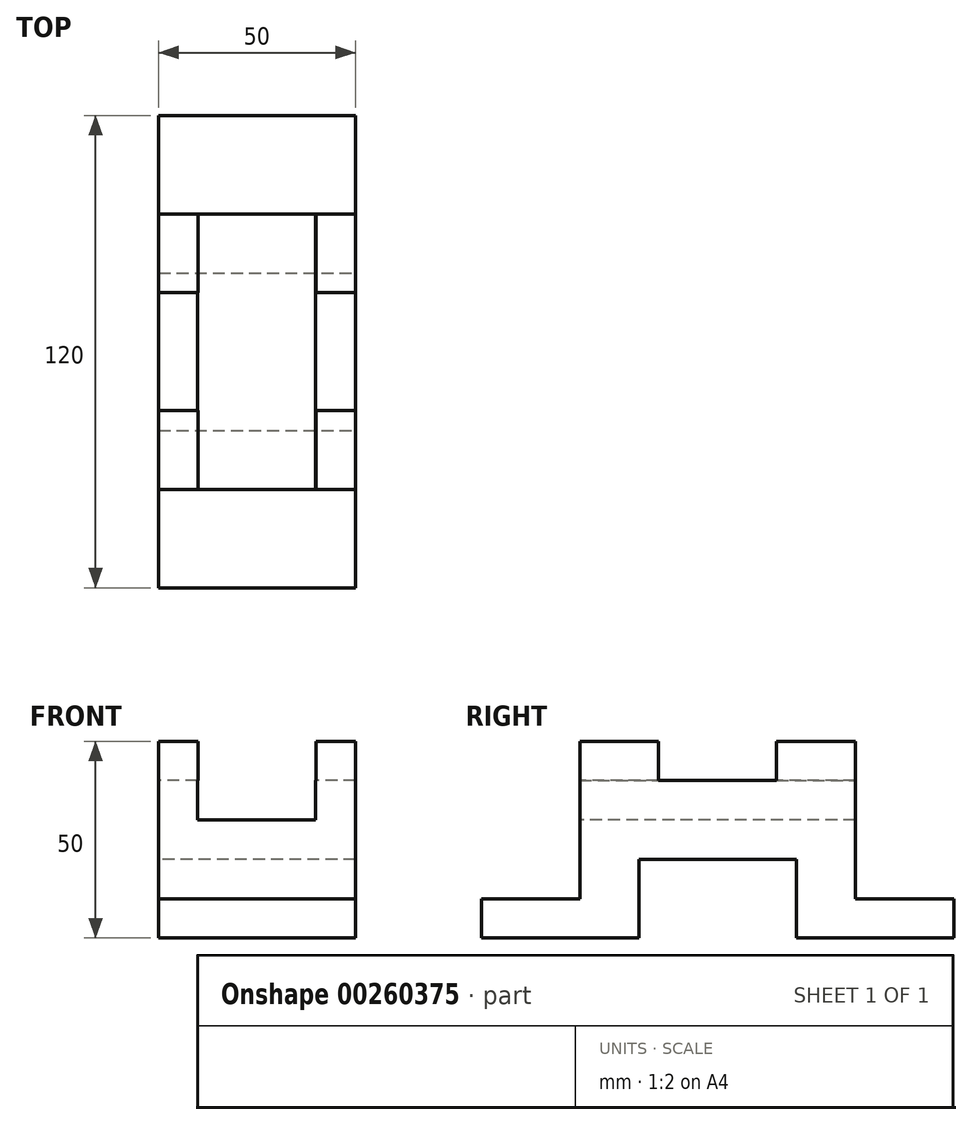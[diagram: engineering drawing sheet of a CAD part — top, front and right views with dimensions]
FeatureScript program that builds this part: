
annotation { "Feature Type Name" : "Feature", "Feature Type Description" : "" }
export const myFeature = defineFeature(function(context is Context, id is Id, definition is map)
    precondition{}
    {
        {
            assignVariable(context, id + "F0", {"name" : "B", "anyValue" : 50 * mm});
        }
        {
            var Q0;
            Q0=qCreatedBy(makeId("Top.planeOp"),FACE);
            var sketch = newSketch(context, id + "F1", { "sketchPlane" : qUnion([Q0])});
            skLineSegment(sketch, "E0.bottom", {"start": v(25, -60) * mm, "end": v(-25, -60) * mm});
            skLineSegment(sketch, "E0.top", {"start": v(25, 60) * mm, "end": v(-25, 60) * mm});
            skLineSegment(sketch, "E0.left", {"start": v(25, -60) * mm, "end": v(25, 60) * mm});
            skLineSegment(sketch, "E0.right", {"start": v(-25, -60) * mm, "end": v(-25, 60) * mm});
            skPoint(sketch, "E0.middle", {"position": v(0, 0) * mm});
            skSolve(sketch);
        }
        {
            var Q0;
            Q0=makeQuery(id+"F1.imprint","IMPRINT",FACE,{"disambiguationData":[TD([[makeQuery(id+"F1.imprint","IMPRINT",EDGE,{"derivedFrom":sQuery(id+"F1.wireOp",EDGE,"E0.bottom")}),-1.0]])]});
            extrude(context, id + "F2", {"entities" : qUnion([Q0]), "depth" : getVariable(context, 'B'), "symmetric" : true});
        }
        {
            var Q0;
            Q0=makeQuery(id+"F2.opExtrude","SWEPT_FACE",FACE,{"disambiguationData":[OSD([sQuery(id+"F1.wireOp",EDGE,"E0.right")])]});
            var sketch = newSketch(context, id + "F3", { "sketchPlane" : qUnion([Q0])});
            skLineSegment(sketch, "E1.bottom", {"start": v(20, -45) * mm, "end": v(-20, -45) * mm});
            skLineSegment(sketch, "E1.top", {"start": v(20, -5) * mm, "end": v(-20, -5) * mm});
            skLineSegment(sketch, "E1.left", {"start": v(20, -45) * mm, "end": v(20, -5) * mm});
            skLineSegment(sketch, "E1.right", {"start": v(-20, -45) * mm, "end": v(-20, -5) * mm});
            skPoint(sketch, "E1.middle", {"position": v(0, -25) * mm});
            skSolve(sketch);
        }
        {
            var Q0;
            Q0 = qSketchRegion(id + "F3", true);
            extrude(context, id + "F4", {"entities" : qUnion([Q0]), "operationType" : NewBodyOperationType.REMOVE, "oppositeDirection" : true, "depth" : 50 * mm});
        }
        {
            var Q0;
            Q0=makeQuery(id+"F2.opExtrude","SWEPT_FACE",FACE,{"disambiguationData":[OSD([sQuery(id+"F1.wireOp",EDGE,"E0.right")])]});
            var sketch = newSketch(context, id + "F5", { "sketchPlane" : qUnion([Q0])});
            skLineSegment(sketch, "E2.bottom", {"start": v(-60, 25) * mm, "end": v(-35, 25) * mm});
            skLineSegment(sketch, "E2.top", {"start": v(-60, -15) * mm, "end": v(-35, -15) * mm});
            skLineSegment(sketch, "E2.left", {"start": v(-60, 25) * mm, "end": v(-60, -15) * mm});
            skLineSegment(sketch, "E2.right", {"start": v(-35, 25) * mm, "end": v(-35, -15) * mm});
            skSolve(sketch);
        }
        {
            var Q0;
            Q0=makeQuery(id+"F5.imprint","IMPRINT",FACE,{"disambiguationData":[TD([[makeQuery(id+"F5.imprint","IMPRINT",EDGE,{"derivedFrom":sQuery(id+"F5.wireOp",EDGE,"E2.bottom")}),1.0]])]});
            extrude(context, id + "F6", {"entities" : qUnion([Q0]), "operationType" : NewBodyOperationType.REMOVE, "oppositeDirection" : true, "depth" : 50 * mm});
        }
        {
            var Q0;
            Q0=makeQuery(id+"F2.opExtrude","SWEPT_FACE",FACE,{"disambiguationData":[OSD([sQuery(id+"F1.wireOp",EDGE,"E0.right")])]});
            var sketch = newSketch(context, id + "F7", { "sketchPlane" : qUnion([Q0])});
            skLineSegment(sketch, "E3.bottom", {"start": v(60, 25) * mm, "end": v(35, 25) * mm});
            skLineSegment(sketch, "E3.top", {"start": v(60, -15) * mm, "end": v(35, -15) * mm});
            skLineSegment(sketch, "E3.left", {"start": v(60, 25) * mm, "end": v(60, -15) * mm});
            skLineSegment(sketch, "E3.right", {"start": v(35, 25) * mm, "end": v(35, -15) * mm});
            skSolve(sketch);
        }
        {
            var Q0;
            Q0=makeQuery(id+"F7.imprint","IMPRINT",FACE,{"disambiguationData":[TD([[makeQuery(id+"F7.imprint","IMPRINT",EDGE,{"derivedFrom":sQuery(id+"F7.wireOp",EDGE,"E3.bottom")}),1.0]])]});
            extrude(context, id + "F8", {"entities" : qUnion([Q0]), "operationType" : NewBodyOperationType.REMOVE, "oppositeDirection" : true, "depth" : 50 * mm});
        }
        {
            var Q0;
            Q0=makeQuery(id+"F2.opExtrude","SWEPT_FACE",FACE,{"disambiguationData":[OSD([sQuery(id+"F1.wireOp",EDGE,"E0.right")])]});
            var sketch = newSketch(context, id + "F9", { "sketchPlane" : qUnion([Q0])});
            skLineSegment(sketch, "E4.bottom", {"start": v(15, 15) * mm, "end": v(-15, 15) * mm});
            skLineSegment(sketch, "E4.top", {"start": v(15, 35) * mm, "end": v(-15, 35) * mm});
            skLineSegment(sketch, "E4.left", {"start": v(15, 15) * mm, "end": v(15, 35) * mm});
            skLineSegment(sketch, "E4.right", {"start": v(-15, 15) * mm, "end": v(-15, 35) * mm});
            skPoint(sketch, "E4.middle", {"position": v(0, 25) * mm});
            skSolve(sketch);
        }
        {
            var Q0;
            {var subQ0=sQuery(id+"F9.wireOp",EDGE,"E4.bottom");Q0=makeQuery(id+"F9.imprint","IMPRINT",FACE,{"disambiguationData":[TD([[makeQuery(id+"F9.imprint","IMPRINT",EDGE,{"derivedFrom":subQ0}),-1.0]])]});}
            extrude(context, id + "F10", {"entities" : qUnion([Q0]), "operationType" : NewBodyOperationType.REMOVE, "oppositeDirection" : true, "depth" : 50 * mm});
        }
        {
            var Q0;
            Q0=makeQuery(id+"F8.boolean.opBoolean","COPY",FACE,{"derivedFrom":makeQuery(id+"F8.opExtrude","SWEPT_FACE",FACE,{"disambiguationData":[OSD([sQuery(id+"F7.wireOp",EDGE,"E3.right")])]})});
            var sketch = newSketch(context, id + "F11", { "sketchPlane" : qUnion([Q0])});
            skLineSegment(sketch, "E5.bottom", {"start": v(15, 15) * mm, "end": v(-15, 15) * mm});
            skLineSegment(sketch, "E5.top", {"start": v(15, 35) * mm, "end": v(-15, 35) * mm});
            skLineSegment(sketch, "E5.left", {"start": v(15, 15) * mm, "end": v(15, 35) * mm});
            skLineSegment(sketch, "E5.right", {"start": v(-15, 15) * mm, "end": v(-15, 35) * mm});
            skPoint(sketch, "E5.middle", {"position": v(0, 25) * mm});
            skSolve(sketch);
        }
        {
            var Q0;
            {var subQ0=sQuery(id+"F11.wireOp",EDGE,"E5.bottom");Q0=makeQuery(id+"F11.imprint","IMPRINT",FACE,{"disambiguationData":[TD([[makeQuery(id+"F11.imprint","IMPRINT",EDGE,{"derivedFrom":subQ0}),-1.0]])]});}
            extrude(context, id + "F12", {"entities" : qUnion([Q0]), "operationType" : NewBodyOperationType.REMOVE, "oppositeDirection" : true, "depth" : 70 * mm});
        }
        {
            var Q0;
            {var subQ0=sQuery(id+"F11.wireOp",EDGE,"E5.bottom");Q0=makeQuery(id+"F11.imprint","IMPRINT",FACE,{"disambiguationData":[TD([[makeQuery(id+"F11.imprint","IMPRINT",EDGE,{"derivedFrom":subQ0}),-1.0]])]});}
            var sketch = newSketch(context, id + "F13", { "sketchPlane" : qUnion([Q0])});
            skLineSegment(sketch, "E6", {"start": v(14.84, 15.04) * mm, "end": v(14.84, 5.04) * mm});
            skLineSegment(sketch, "E7", {"start": v(14.84, 5.04) * mm, "end": v(-15.16, 5.04) * mm});
            skLineSegment(sketch, "E8", {"start": v(-15.16, 5.04) * mm, "end": v(-15.16, 15.04) * mm});
            skLineSegment(sketch, "E9", {"start": v(-15.16, 15.04) * mm, "end": v(14.84, 15.04) * mm});
            skSolve(sketch);
        }
        {
            var Q0;
            Q0 = qSketchRegion(id + "F13", true);
            extrude(context, id + "F14", {"entities" : qUnion([Q0]), "operationType" : NewBodyOperationType.REMOVE, "oppositeDirection" : true, "depth" : 70 * mm});
        }
    });
